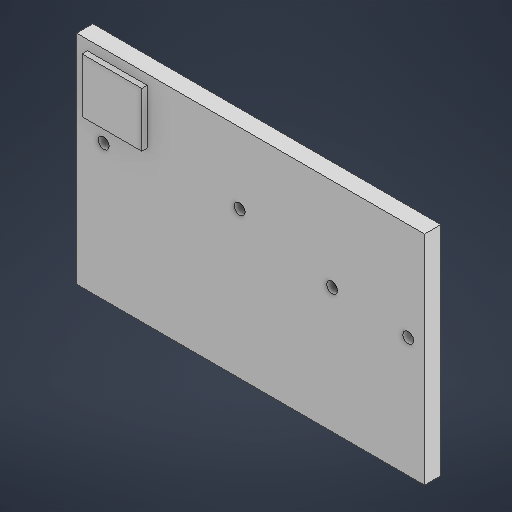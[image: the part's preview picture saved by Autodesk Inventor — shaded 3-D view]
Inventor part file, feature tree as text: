
AUTODESK INVENTOR PART (.ipt)
format: ipt  version: 2025 (Build 290162000, 162)  size: 209,920 bytes
history: native  units: mm
features: extrude x3, sketch x3
ambient origin geometry x8: Origin, YZ Plane, XZ Plane, XY Plane, X Axis, Y Axis, Z Axis, Center Point
bodies: 实体1 (feature_tree)
feature tree (6):
  extrude  "拉伸1"  Depth=40.0mm
  extrude  "拉伸2"  Depth=2.0mm
  extrude  "拉伸3"  Depth=2.0mm
  sketch  "草图1"  dims[d0=64.0mm d1=40.0mm]
  sketch  "草图3"  dims[d2=2.0mm d3=30.0mm]
  sketch  "草图4"  dims[d4=3.0mm d5=0.0mm d10=2.0mm d11=5.0mm d12=15.0mm d13=2.0mm d14=25.0mm d16=2.0mm d17=2.0mm d19=4.0mm d20=17.0mm d21=2.0mm d22=1.0mm d23=3.0mm d24=14.0mm d25=10.0mm d26=0.0mm d27=2.0mm d28=10.0mm d29=11.0mm d30=1.0mm d31=0.0mm]
